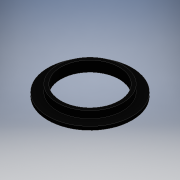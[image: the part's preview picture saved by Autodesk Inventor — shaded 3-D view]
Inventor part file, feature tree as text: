
AUTODESK INVENTOR PART (.ipt)
format: ipt  version: 2016 (Build 200138000, 138)  size: 105,472 bytes
history: native  units: mm
features: extrude x2, other x1, sketch x1
ambient origin geometry x8: Origin, YZ Plane, XZ Plane, XY Plane, X Axis, Y Axis, Z Axis, Center Point
bodies: Body1 (feature_tree)
feature tree (4):
  other  "ソリッド1"
  sketch  "スケッチ1"
  extrude  "押し出し1"  Depth=25.0mm
  extrude  "押し出し2"  Depth=28.0mm
